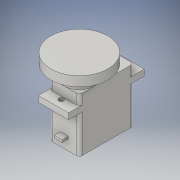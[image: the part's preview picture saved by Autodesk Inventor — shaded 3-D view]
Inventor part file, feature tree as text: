
AUTODESK INVENTOR PART (.ipt)
format: ipt  version: 2016 (Build 200138000, 138)  size: 162,816 bytes
history: native  units: in
note: dims shown in document units (in); Inventor stores cm internally (conversion verified against a paired STEP export)
features: extrude x5, sketch x5, plane x1
ambient origin geometry x8: Origin, YZ Plane, XZ Plane, XY Plane, X Axis, Y Axis, Z Axis, Center Point
bodies: Solid1 (feature_tree)
feature tree (11):
  extrude  "Extrusion1"  Depth=0.9in
  extrude  "Extrusion2"  Depth=0.9in TaperAngle=0.0deg
  extrude  "Extrusion3"  Depth=0.2in
  plane  "Work Plane1"
  extrude  "Extrusion4"  [1 undecoded]
  extrude  "Extrusion5"  Depth=0.08in
  sketch  "Sketch1"  dims[d0=0.5in d1=0.9in]
  sketch  "Sketch2"  dims[d2=0.05in d3=0.9in d4=0.0in]
  sketch  "Sketch3"  dims[d7=0.2in d8=0.0in d9=0.95in]
  sketch  "Sketch5"  dims[d10=0.16in d11=0.0in d12=-0.17in]
  sketch  "Sketch6"  dims[d13=0.63in d14=0.08in d15=1.0in d16=0.1in d17=0.0in d18=0.13in d19=0.04in d20=0.17in d21=0.1in d22=0.0in]
note: 1 required parameter value undecoded (feature->parameter linkage not recoverable at this tier; creation-order binding heuristic only, values carry confidence <= 0.55)
